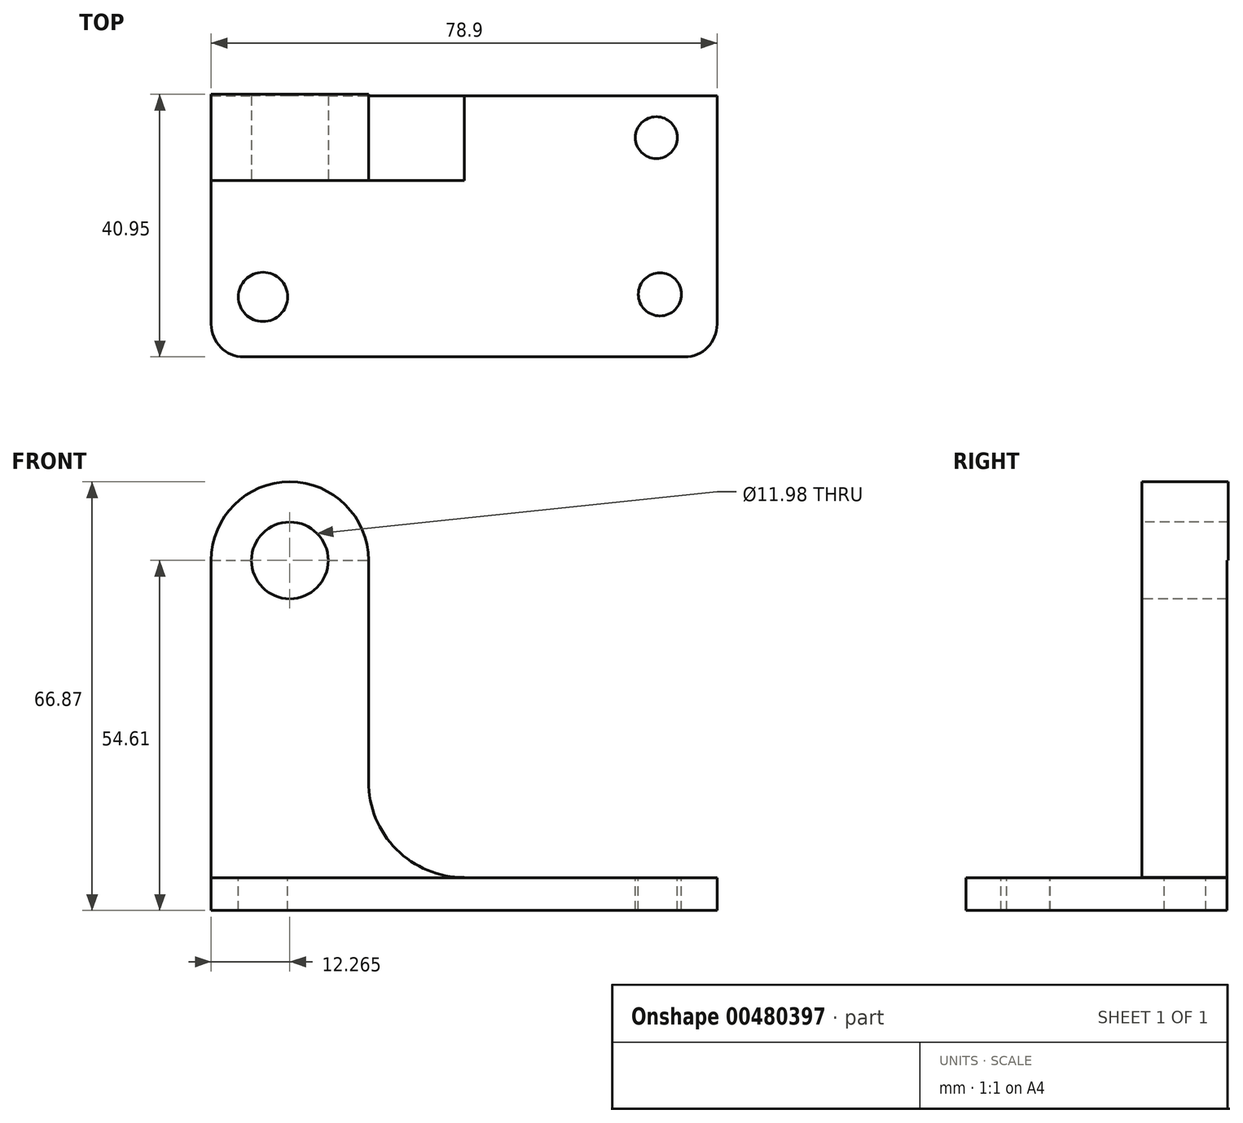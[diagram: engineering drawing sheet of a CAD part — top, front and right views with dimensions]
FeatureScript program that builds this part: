
annotation { "Feature Type Name" : "Feature", "Feature Type Description" : "" }
export const myFeature = defineFeature(function(context is Context, id is Id, definition is map)
    precondition{}
    {
        {
            var Q0;
            Q0=qCreatedBy(makeId("Top.planeOp"),FACE);
            var sketch = newSketch(context, id + "F0", { "sketchPlane" : qUnion([Q0])});
            skLineSegment(sketch, "E0.bottom", {"start": v(-39.45, 20.35) * mm, "end": v(39.45, 20.35) * mm});
            skLineSegment(sketch, "E0.top", {"start": v(-39.45, -20.35) * mm, "end": v(39.45, -20.35) * mm});
            skLineSegment(sketch, "E0.left", {"start": v(-39.45, 20.35) * mm, "end": v(-39.45, -20.35) * mm});
            skLineSegment(sketch, "E0.right", {"start": v(39.45, 20.35) * mm, "end": v(39.45, -20.35) * mm});
            skPoint(sketch, "E0.middle", {"position": v(0, 0) * mm});
            skSolve(sketch);
        }
        {
            var Q0;
            Q0=makeQuery(id+"F0.imprint","IMPRINT",FACE,{"disambiguationData":[TD([[makeQuery(id+"F0.imprint","IMPRINT",EDGE,{"derivedFrom":sQuery(id+"F0.wireOp",EDGE,"E0.bottom")}),-1.0]])]});
            extrude(context, id + "F1", {"entities" : qUnion([Q0]), "depth" : 5.08 * mm});
        }
        {
            var Q0;
            Q0=makeQuery(id+"F1.opExtrude","SWEPT_EDGE",EDGE,{"disambiguationData":[OSD([sQuery(id+"F0.wireOp",EDGE,"E0.top"),sQuery(id+"F0.wireOp",EDGE,"E0.left")])]});
            var Q1;
            Q1=makeQuery(id+"F1.opExtrude","SWEPT_EDGE",EDGE,{"disambiguationData":[OSD([sQuery(id+"F0.wireOp",EDGE,"E0.top"),sQuery(id+"F0.wireOp",EDGE,"E0.right")])]});
            fillet(context, id + "F2", {"entities" : qUnion([Q0, Q1]), "radius" : 5.08 * mm, "tangentPropagation" : true, "allowEdgeOverflow" : false});
        }
        {
            var Q0;
            Q0=makeQuery(id+"F1.opExtrude","CAP_FACE",FACE,{"disambiguationData":[OSD([sQuery(id+"F0.wireOp",EDGE,"E0.bottom"),sQuery(id+"F0.wireOp",EDGE,"E0.top"),sQuery(id+"F0.wireOp",EDGE,"E0.left"),sQuery(id+"F0.wireOp",EDGE,"E0.right")])],"isStart":false});
            var sketch = newSketch(context, id + "F3", { "sketchPlane" : qUnion([Q0])});
            skPoint(sketch, "E1", {"position": v(-31.36, -11) * mm});
            skPoint(sketch, "E2", {"position": v(30.53, -10.6) * mm});
            skPoint(sketch, "E3", {"position": v(29.97, 13.84) * mm});
            skCircle(sketch, "E4", {"center": v(29.97, 13.84) * mm, "radius": 3.26 * mm});
            skCircle(sketch, "E5", {"center": v(30.53, -10.6) * mm, "radius": 3.36 * mm});
            skCircle(sketch, "E6", {"center": v(-31.36, -11) * mm, "radius": 3.84 * mm});
            skSolve(sketch);
        }
        {
            var Q0;
            Q0=makeQuery(id+"F3.imprint","IMPRINT",FACE,{"disambiguationData":[TD([[makeQuery(id+"F3.imprint","IMPRINT",EDGE,{"derivedFrom":sQuery(id+"F3.wireOp",EDGE,"E4")}),1.0]])]});
            var Q1;
            Q1=makeQuery(id+"F3.imprint","IMPRINT",FACE,{"disambiguationData":[TD([[makeQuery(id+"F3.imprint","IMPRINT",EDGE,{"derivedFrom":sQuery(id+"F3.wireOp",EDGE,"E5")}),1.0]])]});
            var Q2;
            Q2=makeQuery(id+"F3.imprint","IMPRINT",FACE,{"disambiguationData":[TD([[makeQuery(id+"F3.imprint","IMPRINT",EDGE,{"derivedFrom":sQuery(id+"F3.wireOp",EDGE,"E6")}),1.0]])]});
            extrude(context, id + "F4", {"entities" : qUnion([Q0, Q1, Q2]), "operationType" : NewBodyOperationType.REMOVE, "oppositeDirection" : true, "depth" : 25.4 * mm});
        }
        {
            var Q0;
            Q0=makeQuery(id+"F1.opExtrude","CAP_FACE",FACE,{"disambiguationData":[OSD([sQuery(id+"F0.wireOp",EDGE,"E0.bottom"),sQuery(id+"F0.wireOp",EDGE,"E0.top"),sQuery(id+"F0.wireOp",EDGE,"E0.left"),sQuery(id+"F0.wireOp",EDGE,"E0.right")])],"isStart":false});
            var sketch = newSketch(context, id + "F5", { "sketchPlane" : qUnion([Q0])});
            skLineSegment(sketch, "E7.bottom", {"start": v(-39.45, 20.35) * mm, "end": v(0, 20.35) * mm});
            skLineSegment(sketch, "E7.top", {"start": v(-39.45, 7.14) * mm, "end": v(0, 7.14) * mm});
            skLineSegment(sketch, "E7.left", {"start": v(-39.45, 20.35) * mm, "end": v(-39.45, 7.14) * mm});
            skLineSegment(sketch, "E7.right", {"start": v(0, 20.35) * mm, "end": v(0, 7.14) * mm});
            skSolve(sketch);
        }
        {
            var Q0;
            Q0 = qSketchRegion(id + "F5", true);
            extrude(context, id + "F6", {"entities" : qUnion([Q0]), "operationType" : NewBodyOperationType.ADD, "depth" : 49.53 * mm});
        }
        {
            var Q0;
            Q0=makeQuery(id+"F6.opExtrude","SWEPT_FACE",FACE,{"disambiguationData":[OSD([sQuery(id+"F5.wireOp",EDGE,"E7.top")])]});
            var sketch = newSketch(context, id + "F7", { "sketchPlane" : qUnion([Q0])});
            skCircle(sketch, "E8", {"center": v(0, 20.07) * mm, "radius": 14.92 * mm});
            skLineSegment(sketch, "E9.bottom", {"start": v(0, 54.6) * mm, "end": v(-14.92, 54.6) * mm});
            skLineSegment(sketch, "E9.top", {"start": v(0, 20.12) * mm, "end": v(-14.92, 20.12) * mm});
            skLineSegment(sketch, "E9.left", {"start": v(0, 54.6) * mm, "end": v(0, 20.12) * mm});
            skLineSegment(sketch, "E9.right", {"start": v(-14.92, 54.6) * mm, "end": v(-14.92, 20.12) * mm});
            skSolve(sketch);
        }
        {
            var Q0;
            {var subQ0=sQuery(id+"F7.wireOp",EDGE,"E9.top");Q0=makeQuery(id+"F7.imprint","IMPRINT",FACE,{"disambiguationData":[TD([[makeQuery(id+"F7.imprint","IMPRINT",EDGE,{"derivedFrom":subQ0}),-1.0]])]});}
            var Q1;
            {var subQ4=sQuery(id+"F7.wireOp",EDGE,"E9.bottom");Q1=makeQuery(id+"F7.imprint","IMPRINT",FACE,{"disambiguationData":[TD([[makeQuery(id+"F7.imprint","IMPRINT",EDGE,{"derivedFrom":subQ4}),-1.0]])]});}
            var Q2;
            {var subQ0=sQuery(id+"F7.wireOp",EDGE,"E9.top");Q2=makeQuery(id+"F7.imprint","IMPRINT",FACE,{"disambiguationData":[TD([[makeQuery(id+"F7.imprint","IMPRINT",EDGE,{"derivedFrom":subQ0}),1.0]])]});}
            var Q3;
            {var subQ0=sQuery(id+"F7.wireOp",EDGE,"E9.left");var subQ1=sQuery(id+"F7.wireOp",EDGE,"E8");var subQ2=makeQuery(id+"F7.imprint","INTERSECT",VERTEX,{"derivedFrom":[subQ1,subQ0]});Q3=makeQuery(id+"F7.imprint","IMPRINT",FACE,{"disambiguationData":[TD([[makeQuery(id+"F7.imprint","IMPRINT",EDGE,{"disambiguationData":[TD([[subQ2,1.0]])],"derivedFrom":subQ1}),1.0]])]});}
            extrude(context, id + "F8", {"entities" : qUnion([Q0, Q1, Q2, Q3]), "operationType" : NewBodyOperationType.REMOVE, "oppositeDirection" : true, "depth" : 25.4 * mm});
        }
        {
            var Q0;
            Q0=makeQuery(id+"F6.opExtrude","SWEPT_FACE",FACE,{"disambiguationData":[OSD([sQuery(id+"F5.wireOp",EDGE,"E7.top")])]});
            var sketch = newSketch(context, id + "F9", { "sketchPlane" : qUnion([Q0])});
            skPoint(sketch, "E10.center.orphan", {"position": v(-27.18, 54.6) * mm});
            skArc(sketch, "E11", {"start": v(-14.92, 54.6) * mm, "mid": v(-27.18, 66.87) * mm, "end": v(-39.45, 54.6) * mm});
            skSolve(sketch);
        }
        {
            var Q0;
            Q0=makeQuery(id+"F9.imprint","IMPRINT",FACE,{"disambiguationData":[TD([[makeQuery(id+"F9.imprint","IMPRINT",EDGE,{"derivedFrom":sQuery(id+"F9.wireOp",EDGE,"E11")}),1.0]])]});
            extrude(context, id + "F10", {"entities" : qUnion([Q0]), "operationType" : NewBodyOperationType.ADD, "oppositeDirection" : true, "depth" : 13.46 * mm});
        }
        {
            var Q0;
            {var subQ0=sQuery(id+"F5.wireOp",EDGE,"E7.top");Q0=makeQuery(id+"F10.boolean.opBoolean","MERGE",FACE,{"derivedFrom":[makeQuery(id+"F6.opExtrude","SWEPT_FACE",FACE,{"disambiguationData":[OSD([subQ0])]}),makeQuery(id+"F10.opExtrude","CAP_FACE",FACE,{"disambiguationData":[OSD([subQ0,sQuery(id+"F9.wireOp",EDGE,"E11")])],"isStart":true})]});}
            var sketch = newSketch(context, id + "F11", { "sketchPlane" : qUnion([Q0])});
            skCircle(sketch, "E12", {"center": v(-27.18, 54.6) * mm, "radius": 5.99 * mm});
            skSolve(sketch);
        }
        {
            var Q0;
            Q0=makeQuery(id+"F11.imprint","IMPRINT",FACE,{"disambiguationData":[TD([[makeQuery(id+"F11.imprint","IMPRINT",EDGE,{"derivedFrom":sQuery(id+"F11.wireOp",EDGE,"E12")}),1.0]])]});
            extrude(context, id + "F12", {"entities" : qUnion([Q0]), "operationType" : NewBodyOperationType.REMOVE, "oppositeDirection" : true, "depth" : 25.4 * mm});
        }
    });
